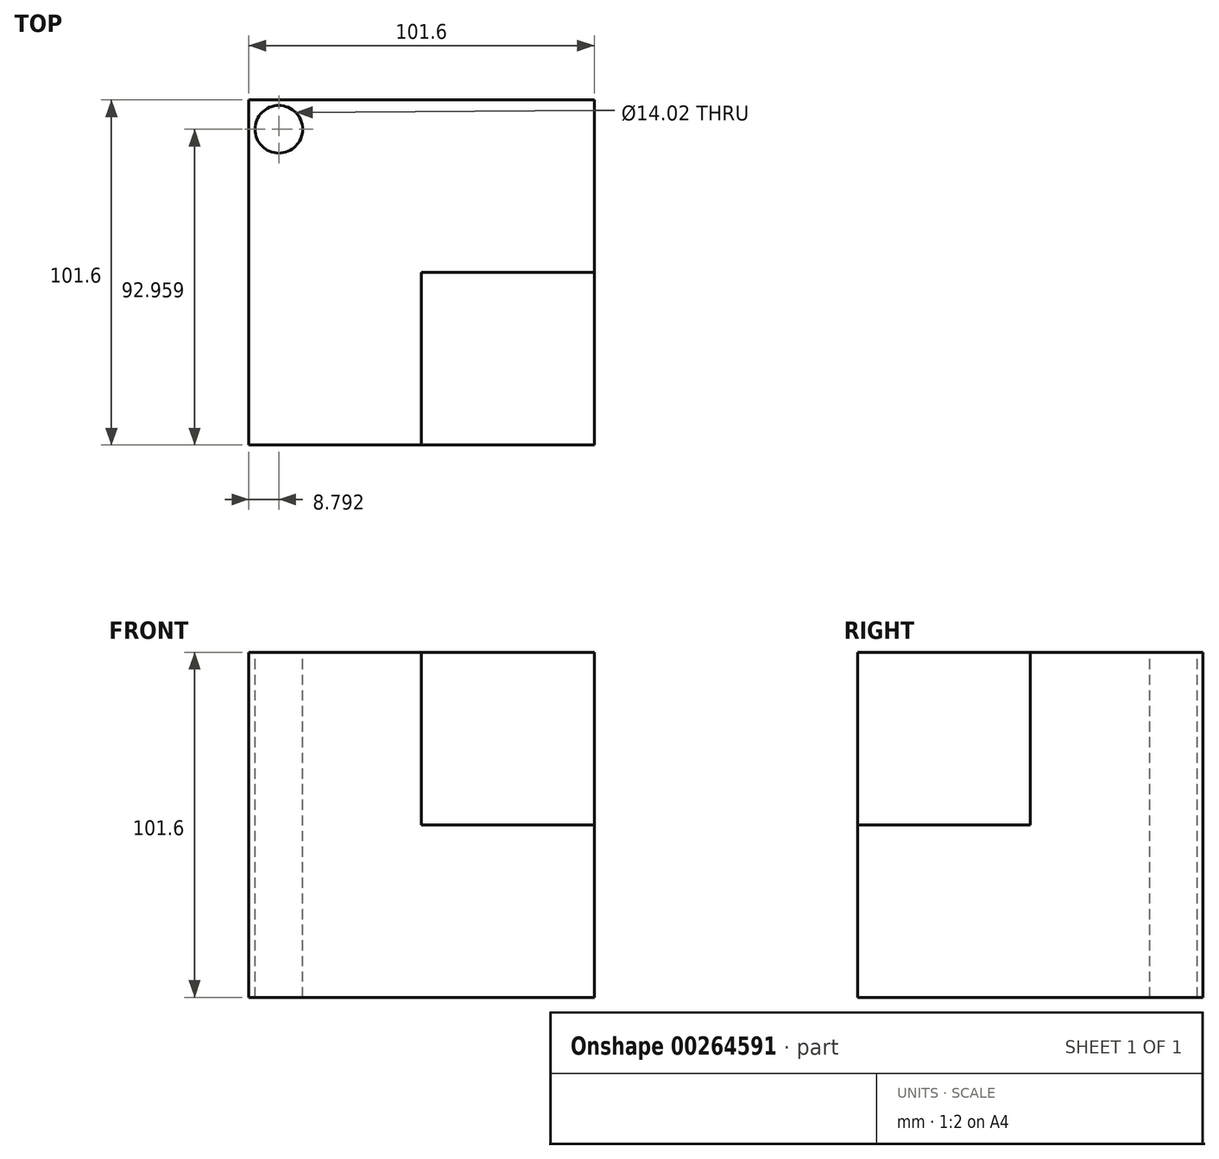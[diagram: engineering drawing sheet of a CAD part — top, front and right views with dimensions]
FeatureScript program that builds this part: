
annotation { "Feature Type Name" : "Feature", "Feature Type Description" : "" }
export const myFeature = defineFeature(function(context is Context, id is Id, definition is map)
    precondition{}
    {
        {
            var Q0;
            Q0=qCreatedBy(makeId("Front.planeOp"),FACE);
            var sketch = newSketch(context, id + "F0", { "sketchPlane" : qUnion([Q0])});
            skLineSegment(sketch, "E0.bottom", {"start": v(0, 0) * mm, "end": v(-101.6, 0) * mm});
            skLineSegment(sketch, "E0.top", {"start": v(0, 101.6) * mm, "end": v(-101.6, 101.6) * mm});
            skLineSegment(sketch, "E0.left", {"start": v(0, 0) * mm, "end": v(0, 101.6) * mm});
            skLineSegment(sketch, "E0.right", {"start": v(-101.6, 0) * mm, "end": v(-101.6, 101.6) * mm});
            skSolve(sketch);
        }
        {
            var Q0;
            Q0 = qSketchRegion(id + "F0", true);
            extrude(context, id + "F1", {"entities" : qUnion([Q0]), "depth" : 101.6 * mm});
        }
        {
            var Q0;
            Q0=makeQuery(id+"F1.opExtrude","SWEPT_FACE",FACE,{"disambiguationData":[OSD([sQuery(id+"F0.wireOp",EDGE,"E0.top")])]});
            var sketch = newSketch(context, id + "F2", { "sketchPlane" : qUnion([Q0])});
            skCircle(sketch, "E1", {"center": v(-92.8, -8.64) * mm, "radius": 7.01 * mm});
            skSolve(sketch);
        }
        {
            var Q0;
            Q0=makeQuery(id+"F2.imprint","IMPRINT",FACE,{"disambiguationData":[TD([[makeQuery(id+"F2.imprint","IMPRINT",EDGE,{"derivedFrom":sQuery(id+"F2.wireOp",EDGE,"E1")}),1.0]])]});
            extrude(context, id + "F3", {"entities" : qUnion([Q0]), "operationType" : NewBodyOperationType.REMOVE, "oppositeDirection" : true, "depth" : 101.6 * mm});
        }
        {
            var Q0;
            Q0=makeQuery(id+"F1.opExtrude","SWEPT_FACE",FACE,{"disambiguationData":[OSD([sQuery(id+"F0.wireOp",EDGE,"E0.top")])]});
            var sketch = newSketch(context, id + "F4", { "sketchPlane" : qUnion([Q0])});
            skLineSegment(sketch, "E2.bottom", {"start": v(0, -101.6) * mm, "end": v(-50.8, -101.6) * mm});
            skLineSegment(sketch, "E2.top", {"start": v(0, -50.8) * mm, "end": v(-50.8, -50.8) * mm});
            skLineSegment(sketch, "E2.left", {"start": v(0, -101.6) * mm, "end": v(0, -50.8) * mm});
            skLineSegment(sketch, "E2.right", {"start": v(-50.8, -101.6) * mm, "end": v(-50.8, -50.8) * mm});
            skSolve(sketch);
        }
        {
            var Q0;
            Q0=makeQuery(id+"F4.imprint","IMPRINT",FACE,{"disambiguationData":[TD([[makeQuery(id+"F4.imprint","IMPRINT",EDGE,{"derivedFrom":sQuery(id+"F4.wireOp",EDGE,"E2.bottom")}),-1.0]])]});
            extrude(context, id + "F5", {"entities" : qUnion([Q0]), "operationType" : NewBodyOperationType.REMOVE, "oppositeDirection" : true, "depth" : 50.8 * mm});
        }
    });
